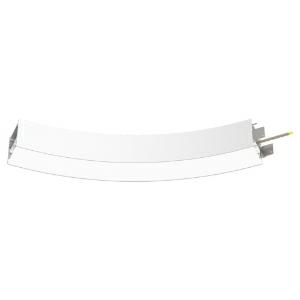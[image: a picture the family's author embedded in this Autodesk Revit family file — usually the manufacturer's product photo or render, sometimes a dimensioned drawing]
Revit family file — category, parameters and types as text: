
# Revit family: super-g_slim_super_g_slim_1550_45deg_ab_ps_led__12w_1580lm_3000k_cri_80_350-1380_8963
name_source: partatom
category: Leuchten
revit_build: Autodesk Revit 2016 (Build: 20190508_0715(x64)
units: mm (PartAtom-declared; Revit-internal decimal feet)

## family parameters
Basisbauteil = Fläche
Beim Laden mit Abzugskörper schneiden = Nein
Bemaßung runder Anschluss = Durchmesser verwenden
Gemeinsam genutzt = Nein
Lichtquelle = Nein
Raumberechnungspunkt = Nein
Teiletyp = Normal

## types (1)
- 350-1380-D01 (1 x LED, 480 lm, 3000K)
    Approval mark = CE
    Beschreibung = The insert consists of aluminum-extruded profile. Charming SOFT-EDGE design ensure unparalleled styling. The ballast is integrated and allows for an operation with 220-240V (50/60Hz). SUPER-G SLIM (# 350-1380) ist not dimmable (on/off).
    CIE Flux Codes = 48 79 96 100 71
    Color Rendering = 1B/80…89
    Color Temperature = 3000K
    Height = 90 mm
    Hersteller = Prolicht
    Lamp Light Flux = 480 lm
    Lamp count = 1
    Lampe = 1 x LED
    Length = 146 mm
    Luminous efficacy = 103 lm/W
    ModVariant = Nein
    Modell = 350-1380
    Mounting Place = Ceiling
    Mounting Type = Surface mounted
    Number of Poles = 1
    OnlyDefault = Ja
    Power Factor = 1
    Product Name = SUPER-G SLIM__SUPER G SLIM 1550/45° AB PS LED: 12W 1580lm 3000K CRI:80
    Product group = Surface profile systems
    ProductGroupID = 335
    Protection Class = Protection class I
    Protection Degree = IP 20
    RLX_Detail_Level = 1
    RlxData = <blob elided: 34021 chars, md5=449bf92d>
    Scheinlast = 13 VA
    Socket = socket
    Standby Power = 0 W
    System Light Flux = 1361 lm
    System Power = 13 W
    Typenbild = 350-1380.jpg
    URL = http://relux.com
    VarID = 350-1380-d01
    Voltage = 0 V
    Vorgabe-Ansicht = 1800 mm
    Weight = 0.00 kg
    Width = 65 mm

## geometry (parser evidence)
native form markers: Blend x4, Sweep x19
no freeform markers — native parametric forms only
